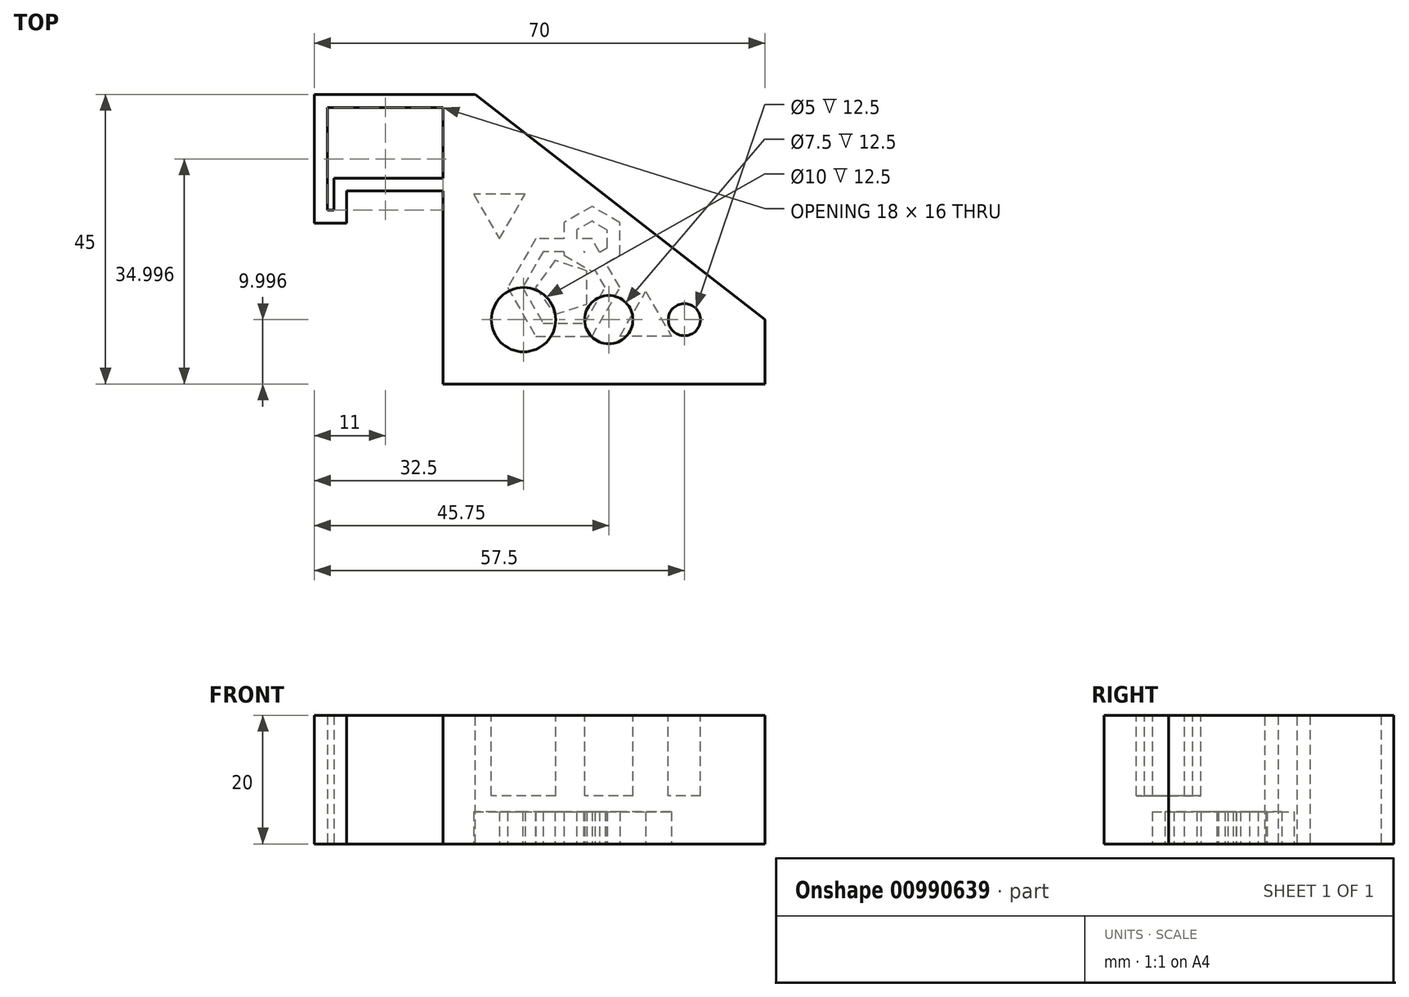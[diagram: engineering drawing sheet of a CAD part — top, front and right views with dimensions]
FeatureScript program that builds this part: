
annotation { "Feature Type Name" : "Feature", "Feature Type Description" : "" }
export const myFeature = defineFeature(function(context is Context, id is Id, definition is map)
    precondition{}
    {
        {
            var Q0;
            Q0=qCreatedBy(makeId("Top.planeOp"),FACE);
            var sketch = newSketch(context, id + "F0", { "sketchPlane" : qUnion([Q0])});
            skLineSegment(sketch, "E0", {"start": v(0, -22.56) * mm, "end": v(50, -22.56) * mm});
            skLineSegment(sketch, "E1", {"start": v(50, -22.56) * mm, "end": v(50, -12.56) * mm});
            skLineSegment(sketch, "E2", {"start": v(5, 22.44) * mm, "end": v(50, -12.56) * mm});
            skLineSegment(sketch, "E3", {"start": v(0, 7.44) * mm, "end": v(0, -22.56) * mm});
            skCircle(sketch, "E4", {"center": v(12.5, -12.56) * mm, "radius": 5 * mm});
            skCircle(sketch, "E5", {"center": v(25.75, -12.56) * mm, "radius": 3.75 * mm});
            skCircle(sketch, "E6", {"center": v(37.5, -12.56) * mm, "radius": 2.5 * mm});
            skLineSegment(sketch, "E7", {"start": v(0, 7.44) * mm, "end": v(-15, 7.44) * mm});
            skLineSegment(sketch, "E8", {"start": v(-15, 7.44) * mm, "end": v(-15, 2.44) * mm});
            skLineSegment(sketch, "E9", {"start": v(-15, 2.44) * mm, "end": v(-20, 2.44) * mm});
            skLineSegment(sketch, "E10", {"start": v(-20, 2.44) * mm, "end": v(-20, 22.44) * mm});
            skLineSegment(sketch, "E11", {"start": v(-20, 22.44) * mm, "end": v(5, 22.44) * mm});
            skSolve(sketch);
        }
        {
            var Q0;
            Q0=makeQuery(id+"F0.imprint","IMPRINT",FACE,{"disambiguationData":[TD([[makeQuery(id+"F0.imprint","IMPRINT",EDGE,{"derivedFrom":sQuery(id+"F0.wireOp",EDGE,"E6")}),1.0]])]});
            var Q1;
            Q1=makeQuery(id+"F0.imprint","IMPRINT",FACE,{"disambiguationData":[TD([[makeQuery(id+"F0.imprint","IMPRINT",EDGE,{"derivedFrom":sQuery(id+"F0.wireOp",EDGE,"E0")}),1.0]])]});
            var Q2;
            Q2=makeQuery(id+"F0.imprint","IMPRINT",FACE,{"disambiguationData":[TD([[makeQuery(id+"F0.imprint","IMPRINT",EDGE,{"derivedFrom":sQuery(id+"F0.wireOp",EDGE,"E5")}),1.0]])]});
            var Q3;
            Q3=makeQuery(id+"F0.imprint","IMPRINT",FACE,{"disambiguationData":[TD([[makeQuery(id+"F0.imprint","IMPRINT",EDGE,{"derivedFrom":sQuery(id+"F0.wireOp",EDGE,"E4")}),1.0]])]});
            extrude(context, id + "F1", {"entities" : qUnion([Q0, Q1, Q2, Q3]), "oppositeDirection" : true, "depth" : 20 * mm, "offsetDistance" : 25 * mm});
        }
        {
            var Q0;
            Q0=makeQuery(id+"F0.imprint","IMPRINT",FACE,{"disambiguationData":[TD([[makeQuery(id+"F0.imprint","IMPRINT",EDGE,{"derivedFrom":sQuery(id+"F0.wireOp",EDGE,"E4")}),1.0]])]});
            var Q1;
            Q1=makeQuery(id+"F0.imprint","IMPRINT",FACE,{"disambiguationData":[TD([[makeQuery(id+"F0.imprint","IMPRINT",EDGE,{"derivedFrom":sQuery(id+"F0.wireOp",EDGE,"E5")}),1.0]])]});
            var Q2;
            Q2=makeQuery(id+"F0.imprint","IMPRINT",FACE,{"disambiguationData":[TD([[makeQuery(id+"F0.imprint","IMPRINT",EDGE,{"derivedFrom":sQuery(id+"F0.wireOp",EDGE,"E6")}),1.0]])]});
            extrude(context, id + "F2", {"entities" : qUnion([Q0, Q1, Q2]), "operationType" : NewBodyOperationType.REMOVE, "endBound" : BoundingType.SYMMETRIC, "oppositeDirection" : true, "depth" : 25 * mm, "offsetDistance" : 25 * mm});
        }
        {
            var Q0;
            Q0=makeQuery(id+"F1.opExtrude","CAP_FACE",FACE,{"disambiguationData":[OSD([sQuery(id+"F0.wireOp",EDGE,"E0"),sQuery(id+"F0.wireOp",EDGE,"E1"),sQuery(id+"F0.wireOp",EDGE,"E2"),sQuery(id+"F0.wireOp",EDGE,"E3"),sQuery(id+"F0.wireOp",EDGE,"E7"),sQuery(id+"F0.wireOp",EDGE,"E8"),sQuery(id+"F0.wireOp",EDGE,"E9"),sQuery(id+"F0.wireOp",EDGE,"E10"),sQuery(id+"F0.wireOp",EDGE,"E11")])],"isStart":false});
            var sketch = newSketch(context, id + "F3", { "sketchPlane" : qUnion([Q0])});
            skCircle(sketch, "E12.cCircle", {"center": v(18.76, 7.56) * mm, "radius": 7.56 * mm, "construction": true});
            skPoint(sketch, "E12.cCircle.centerSnap0", {"position": v(0, 7.56) * mm});
            skLineSegment(sketch, "E12.0", {"start": v(23.13, 0) * mm, "end": v(14.4, 0) * mm});
            skLineSegment(sketch, "E12.1", {"start": v(14.4, 0) * mm, "end": v(10.03, 7.56) * mm});
            skLineSegment(sketch, "E12.2", {"start": v(10.03, 7.56) * mm, "end": v(14.4, 15.13) * mm});
            skLineSegment(sketch, "E12.3", {"start": v(14.4, 15.13) * mm, "end": v(23.13, 15.13) * mm});
            skLineSegment(sketch, "E12.4", {"start": v(23.13, 15.13) * mm, "end": v(27.5, 7.56) * mm});
            skLineSegment(sketch, "E12.5", {"start": v(27.5, 7.56) * mm, "end": v(23.13, 0) * mm});
            skPoint(sketch, "E12.0.midPoint", {"position": v(18.76, 0) * mm});
            skCircle(sketch, "E13.cCircle", {"center": v(23.13, 0) * mm, "radius": 4.37 * mm, "construction": true});
            skPoint(sketch, "E13.cCircle.perimeterSnap0", {"position": v(27.5, -4.94) * mm});
            skLineSegment(sketch, "E13.0", {"start": v(27.5, 2.52) * mm, "end": v(27.5, -2.52) * mm});
            skLineSegment(sketch, "E13.1", {"start": v(27.5, -2.52) * mm, "end": v(23.13, -5.04) * mm});
            skLineSegment(sketch, "E13.2", {"start": v(23.13, -5.04) * mm, "end": v(18.76, -2.52) * mm});
            skLineSegment(sketch, "E13.3", {"start": v(18.76, -2.52) * mm, "end": v(18.76, 2.52) * mm});
            skLineSegment(sketch, "E13.4", {"start": v(18.76, 2.52) * mm, "end": v(23.13, 5.04) * mm});
            skLineSegment(sketch, "E13.5", {"start": v(23.13, 5.04) * mm, "end": v(27.5, 2.52) * mm});
            skPoint(sketch, "E13.0.midPoint", {"position": v(27.5, 0) * mm});
            skPoint(sketch, "E13.0.midPoint.positionSnap0", {"position": v(27.5, -4.94) * mm});
            skCircle(sketch, "E14.cCircle", {"center": v(18.76, 7.56) * mm, "radius": 5.56 * mm, "construction": true});
            skLineSegment(sketch, "E14.0", {"start": v(21.98, 13.13) * mm, "end": v(25.19, 7.56) * mm});
            skLineSegment(sketch, "E14.1", {"start": v(25.19, 7.56) * mm, "end": v(21.98, 2) * mm});
            skLineSegment(sketch, "E14.2", {"start": v(21.98, 2) * mm, "end": v(15.55, 2) * mm});
            skLineSegment(sketch, "E14.3", {"start": v(15.55, 2) * mm, "end": v(12.34, 7.56) * mm});
            skLineSegment(sketch, "E14.4", {"start": v(12.34, 7.56) * mm, "end": v(15.55, 13.13) * mm});
            skLineSegment(sketch, "E14.5", {"start": v(15.55, 13.13) * mm, "end": v(21.98, 13.13) * mm});
            skPoint(sketch, "E14.0.midPoint", {"position": v(23.58, 10.35) * mm});
            skCircle(sketch, "E15.cCircle", {"center": v(23.13, 0) * mm, "radius": 2.37 * mm, "construction": true});
            skLineSegment(sketch, "E15.0", {"start": v(25.5, 1.37) * mm, "end": v(25.5, -1.37) * mm});
            skLineSegment(sketch, "E15.1", {"start": v(25.5, -1.37) * mm, "end": v(23.13, -2.74) * mm});
            skLineSegment(sketch, "E15.2", {"start": v(23.13, -2.74) * mm, "end": v(20.76, -1.37) * mm});
            skLineSegment(sketch, "E15.3", {"start": v(20.76, -1.37) * mm, "end": v(20.76, 1.37) * mm});
            skLineSegment(sketch, "E15.4", {"start": v(20.76, 1.37) * mm, "end": v(23.13, 2.74) * mm});
            skLineSegment(sketch, "E15.5", {"start": v(23.13, 2.74) * mm, "end": v(25.5, 1.37) * mm});
            skPoint(sketch, "E15.0.midPoint", {"position": v(25.5, 0) * mm});
            skCircle(sketch, "E16.cCircle", {"center": v(18.76, 7.56) * mm, "radius": 3.56 * mm, "construction": true});
            skLineSegment(sketch, "E16.0", {"start": v(22.32, 10.16) * mm, "end": v(22.33, 4.98) * mm});
            skLineSegment(sketch, "E16.1", {"start": v(22.33, 4.98) * mm, "end": v(17.41, 3.37) * mm});
            skLineSegment(sketch, "E16.2", {"start": v(17.41, 3.37) * mm, "end": v(14.36, 7.55) * mm});
            skLineSegment(sketch, "E16.3", {"start": v(14.36, 7.55) * mm, "end": v(17.4, 11.75) * mm});
            skLineSegment(sketch, "E16.4", {"start": v(17.4, 11.75) * mm, "end": v(22.32, 10.16) * mm});
            skPoint(sketch, "E16.0.midPoint", {"position": v(22.33, 7.57) * mm});
            skLineSegment(sketch, "E17", {"start": v(27.5, 15.13) * mm, "end": v(31.5, 8.2) * mm});
            skLineSegment(sketch, "E18", {"start": v(31.5, 8.2) * mm, "end": v(35.5, 15.13) * mm});
            skLineSegment(sketch, "E19", {"start": v(35.5, 15.13) * mm, "end": v(27.5, 15.13) * mm});
            skLineSegment(sketch, "E20", {"start": v(8.75, 0) * mm, "end": v(12.75, -6.93) * mm});
            skLineSegment(sketch, "E21", {"start": v(12.75, -6.93) * mm, "end": v(4.75, -6.93) * mm});
            skLineSegment(sketch, "E22", {"start": v(4.75, -6.93) * mm, "end": v(8.75, 0) * mm});
            skLineSegment(sketch, "E23.bottom", {"start": v(-15, -9.44) * mm, "end": v(0, -9.44) * mm});
            skLineSegment(sketch, "E23.top", {"start": v(-15, -20.44) * mm, "end": v(0, -20.44) * mm});
            skLineSegment(sketch, "E23.right", {"start": v(0, -9.44) * mm, "end": v(0, -20.44) * mm});
            skLineSegment(sketch, "E24", {"start": v(-15, -20.44) * mm, "end": v(-18, -20.44) * mm});
            skLineSegment(sketch, "E25", {"start": v(-18, -20.44) * mm, "end": v(-18, -4.44) * mm});
            skLineSegment(sketch, "E26", {"start": v(-18, -4.44) * mm, "end": v(-17, -4.44) * mm});
            skLineSegment(sketch, "E27", {"start": v(-17, -4.44) * mm, "end": v(-17, -9.44) * mm});
            skLineSegment(sketch, "E28", {"start": v(-17, -9.44) * mm, "end": v(-15, -9.44) * mm});
            skSolve(sketch);
        }
        {
            var Q0;
            {var subQ12=sQuery(id+"F3.wireOp",EDGE,"E13.0");Q0=makeQuery(id+"F3.imprint","IMPRINT",FACE,{"disambiguationData":[TD([[makeQuery(id+"F3.imprint","IMPRINT",EDGE,{"derivedFrom":subQ12}),-1.0]])]});}
            var Q1;
            {var subQ5=sQuery(id+"F3.wireOp",EDGE,"E12.0");var subQ7=sQuery(id+"F3.wireOp",EDGE,"E15.3");var subQ9=makeQuery(id+"F3.imprint","INTERSECT",VERTEX,{"derivedFrom":[subQ5,subQ7]});Q1=makeQuery(id+"F3.imprint","IMPRINT",FACE,{"disambiguationData":[TD([[makeQuery(id+"F3.imprint","IMPRINT",EDGE,{"disambiguationData":[TD([[subQ9,-1.0]])],"derivedFrom":subQ5}),-1.0]])]});}
            var Q2;
            {var subQ7=sQuery(id+"F3.wireOp",EDGE,"E12.0");var subQ10=sQuery(id+"F3.wireOp",EDGE,"E12.5");var subQ11=makeQuery(id+"F3.imprint","INTERSECT",VERTEX,{"derivedFrom":[subQ7,subQ10]});Q2=makeQuery(id+"F3.imprint","IMPRINT",FACE,{"disambiguationData":[TD([[makeQuery(id+"F3.imprint","IMPRINT",EDGE,{"disambiguationData":[TD([[subQ11,-1.0]])],"derivedFrom":subQ7}),-1.0]])]});}
            var Q3;
            {var subQ5=sQuery(id+"F3.wireOp",EDGE,"E13.5");var subQ7=sQuery(id+"F3.wireOp",EDGE,"E12.5");var subQ8=makeQuery(id+"F3.imprint","INTERSECT",VERTEX,{"derivedFrom":[subQ7,subQ5]});Q3=makeQuery(id+"F3.imprint","IMPRINT",FACE,{"disambiguationData":[TD([[makeQuery(id+"F3.imprint","IMPRINT",EDGE,{"disambiguationData":[TD([[subQ8,-1.0]])],"derivedFrom":subQ7}),-1.0]])]});}
            var Q4;
            {var subQ5=sQuery(id+"F3.wireOp",EDGE,"E13.4");Q4=makeQuery(id+"F3.imprint","IMPRINT",FACE,{"disambiguationData":[TD([[makeQuery(id+"F3.imprint","IMPRINT",EDGE,{"derivedFrom":subQ5}),-1.0]])]});}
            var Q5;
            {var subQ7=sQuery(id+"F3.wireOp",EDGE,"E12.1");Q5=makeQuery(id+"F3.imprint","IMPRINT",FACE,{"disambiguationData":[TD([[makeQuery(id+"F3.imprint","IMPRINT",EDGE,{"derivedFrom":subQ7}),-1.0]])]});}
            var Q6;
            Q6=makeQuery(id+"F3.imprint","IMPRINT",FACE,{"disambiguationData":[TD([[makeQuery(id+"F3.imprint","IMPRINT",EDGE,{"derivedFrom":sQuery(id+"F3.wireOp",EDGE,"E20")}),-1.0]])]});
            var Q7;
            Q7=makeQuery(id+"F3.imprint","IMPRINT",FACE,{"disambiguationData":[TD([[makeQuery(id+"F3.imprint","IMPRINT",EDGE,{"derivedFrom":sQuery(id+"F3.wireOp",EDGE,"E17")}),1.0]])]});
            var Q8;
            Q8=makeQuery(id+"F3.imprint","IMPRINT",FACE,{"disambiguationData":[TD([[makeQuery(id+"F3.imprint","IMPRINT",EDGE,{"derivedFrom":sQuery(id+"F3.wireOp",EDGE,"E16.0")}),-1.0]])]});
            extrude(context, id + "F4", {"entities" : qUnion([Q0, Q1, Q2, Q3, Q4, Q5, Q6, Q7, Q8]), "operationType" : NewBodyOperationType.REMOVE, "oppositeDirection" : true, "depth" : 5 * mm, "offsetDistance" : 25 * mm});
        }
        {
            var Q0;
            Q0=makeQuery(id+"F3.imprint","IMPRINT",FACE,{"disambiguationData":[TD([[makeQuery(id+"F3.imprint","IMPRINT",EDGE,{"derivedFrom":sQuery(id+"F3.wireOp",EDGE,"E23.bottom")}),-1.0]])]});
            extrude(context, id + "F5", {"entities" : qUnion([Q0]), "operationType" : NewBodyOperationType.REMOVE, "endBound" : BoundingType.THROUGH_ALL, "oppositeDirection" : true, "depth" : 25 * mm, "offsetDistance" : 25 * mm});
        }
    });
